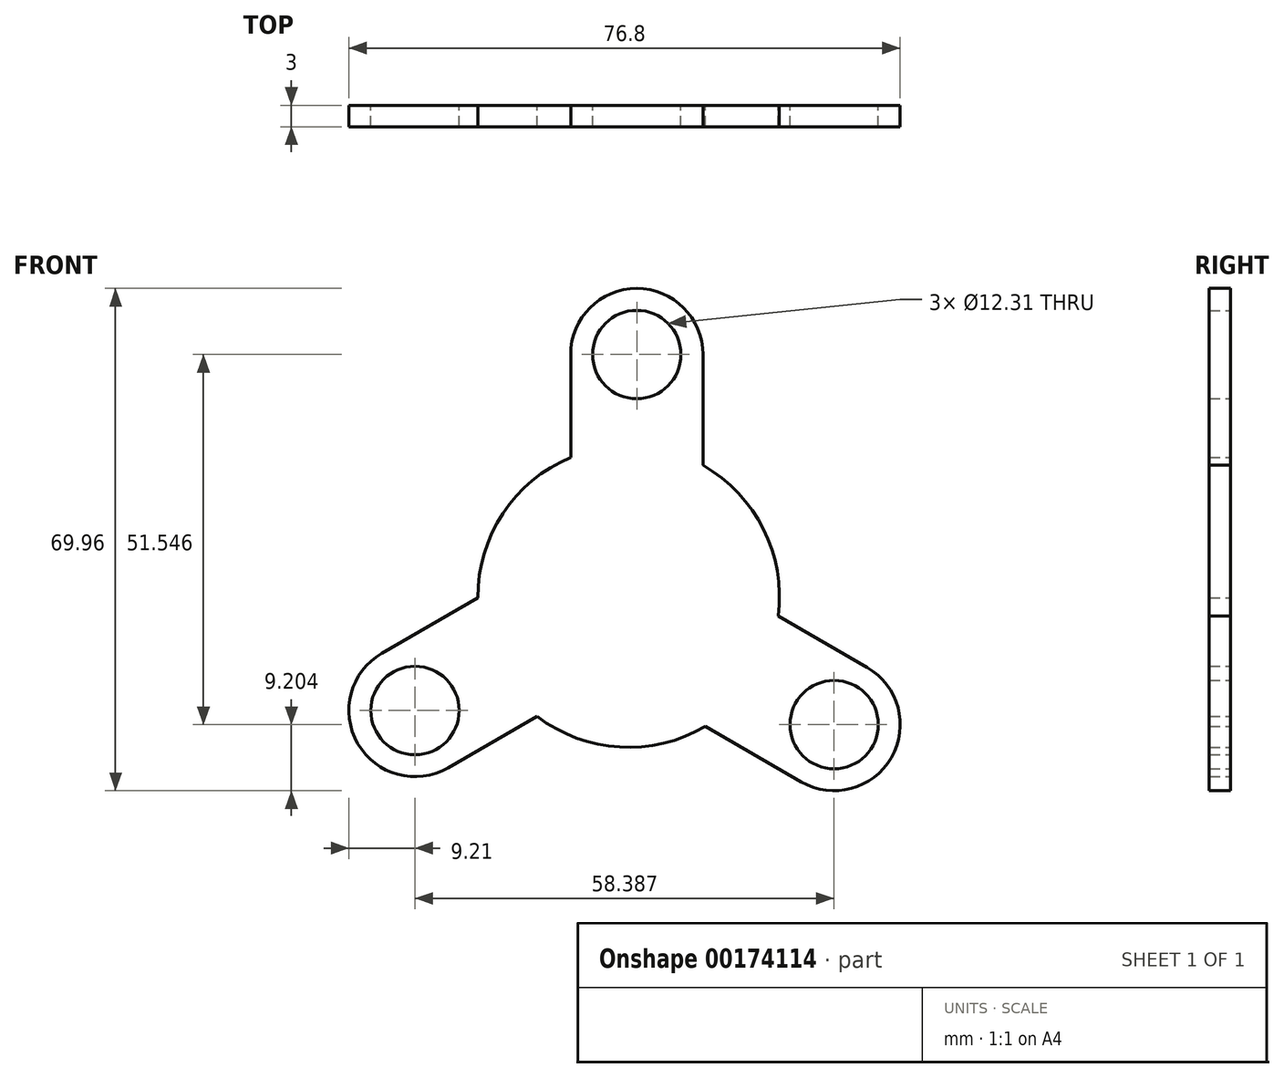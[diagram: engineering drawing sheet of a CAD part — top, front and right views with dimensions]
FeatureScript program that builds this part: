
annotation { "Feature Type Name" : "Feature", "Feature Type Description" : "" }
export const myFeature = defineFeature(function(context is Context, id is Id, definition is map)
    precondition{}
    {
        {
            var Q0;
            Q0=qCreatedBy(makeId("Front.planeOp"),FACE);
            var sketch = newSketch(context, id + "F0", { "sketchPlane" : qUnion([Q0])});
            skArc(sketch, "E0", {"start": v(-8.07, 19.39) * mm, "mid": v(-17.52, 11.57) * mm, "end": v(-21, -0.18) * mm});
            skLineSegment(sketch, "E1.left", {"start": v(-8.07, 33.7) * mm, "end": v(-8.07, 19.39) * mm});
            skLineSegment(sketch, "E1.right", {"start": v(10.34, 33.7) * mm, "end": v(10.34, 18.28) * mm});
            skArc(sketch, "E2", {"start": v(10.34, 33.7) * mm, "mid": v(1.13, 42.92) * mm, "end": v(-8.07, 33.7) * mm});
            skLineSegment(sketch, "E3.1.0", {"start": v(-25.16, -23.85) * mm, "end": v(-12.75, -16.68) * mm});
            skArc(sketch, "E3.1.1", {"start": v(-34.36, -7.9) * mm, "mid": v(-37.73, -20.48) * mm, "end": v(-25.16, -23.85) * mm});
            skLineSegment(sketch, "E3.1.2", {"start": v(-34.36, -7.9) * mm, "end": v(-21, -0.18) * mm});
            skLineSegment(sketch, "E3.2.0", {"start": v(33.23, -9.86) * mm, "end": v(20.83, -2.7) * mm});
            skArc(sketch, "E3.2.1", {"start": v(24.02, -25.8) * mm, "mid": v(36.6, -22.44) * mm, "end": v(33.23, -9.86) * mm});
            skLineSegment(sketch, "E3.2.2", {"start": v(24.02, -25.8) * mm, "end": v(10.66, -18.1) * mm});
            skArc(sketch, "E4.trimOffspring", {"start": v(20.83, -2.7) * mm, "mid": v(18.78, 9.39) * mm, "end": v(10.34, 18.28) * mm});
            skArc(sketch, "E5.trimOffspring", {"start": v(-12.75, -16.68) * mm, "mid": v(-1.26, -20.96) * mm, "end": v(10.66, -18.1) * mm});
            skCircle(sketch, "E6", {"center": v(1.13, 33.7) * mm, "radius": 6.16 * mm});
            skCircle(sketch, "E7", {"center": v(1.13, 33.7) * mm, "radius": 3.12 * mm});
            skCircle(sketch, "E8.1.0", {"center": v(-29.76, -15.87) * mm, "radius": 6.16 * mm});
            skCircle(sketch, "E8.2.0", {"center": v(28.63, -17.84) * mm, "radius": 6.16 * mm});
            skCircle(sketch, "E9.1.0", {"center": v(-29.76, -15.87) * mm, "radius": 3.12 * mm});
            skCircle(sketch, "E9.2.0", {"center": v(28.63, -17.84) * mm, "radius": 3.12 * mm});
            skSolve(sketch);
        }
        {
            var Q0;
            Q0 = qSketchRegion(id + "F0", true);
            extrude(context, id + "F1", {"entities" : qUnion([Q0]), "depth" : 3 * mm});
        }
    });
